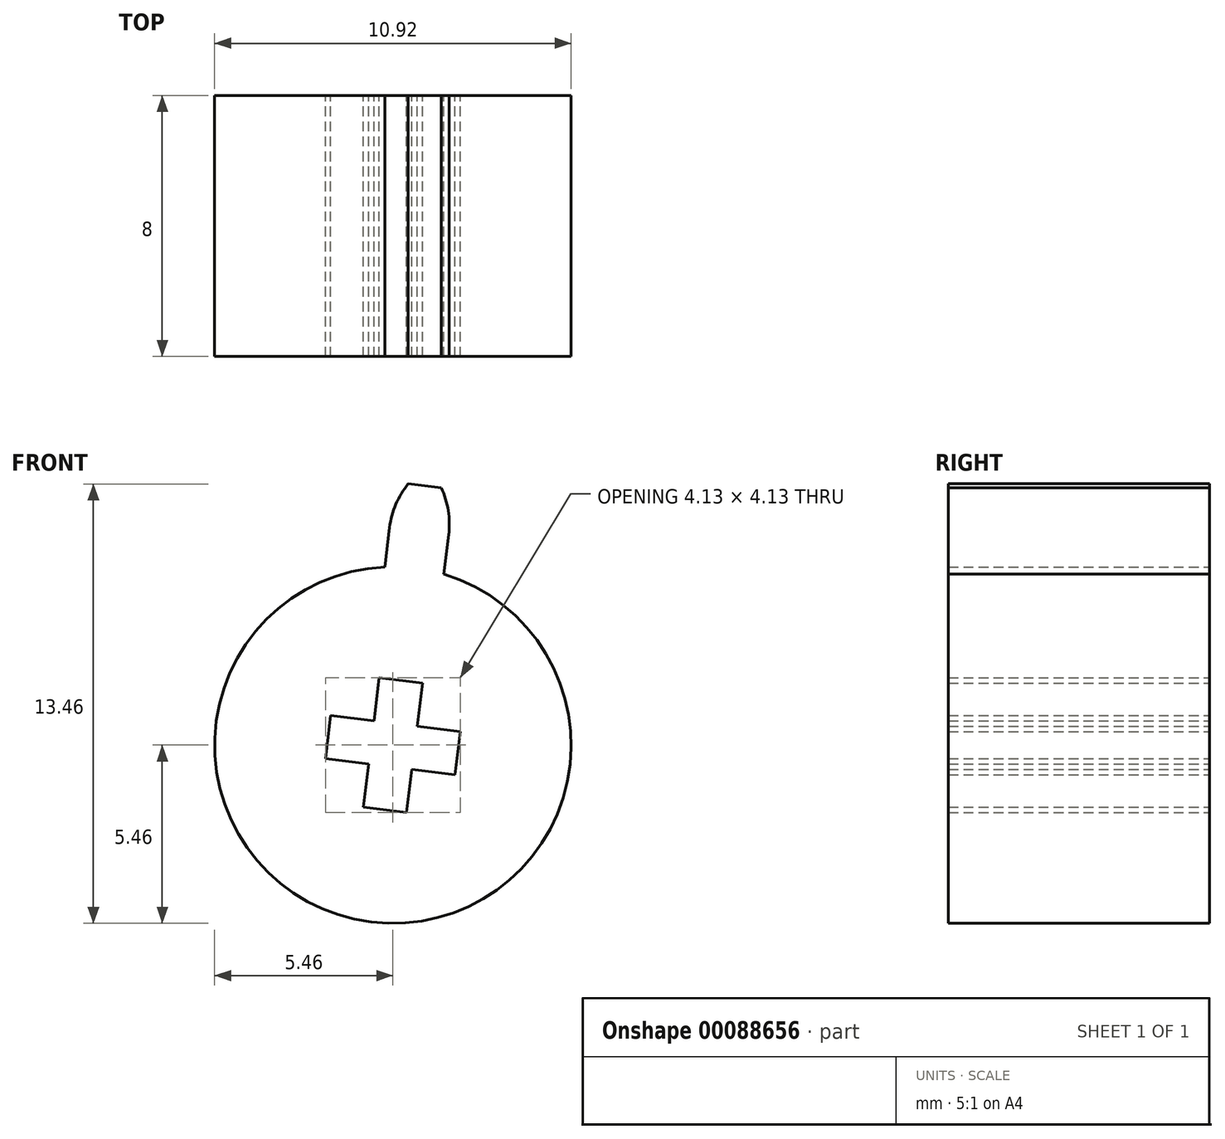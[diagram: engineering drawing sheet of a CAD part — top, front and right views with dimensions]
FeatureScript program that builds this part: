
annotation { "Feature Type Name" : "Feature", "Feature Type Description" : "" }
export const myFeature = defineFeature(function(context is Context, id is Id, definition is map)
    precondition{}
    {
        {
            var Q0;
            Q0=qCreatedBy(makeId("Front.planeOp"),FACE);
            var sketch = newSketch(context, id + "F0", { "sketchPlane" : qUnion([Q0])});
            skLineSegment(sketch, "E0", {"start": v(0.47, 8) * mm, "end": v(1.48, 7.88) * mm});
            skArc(sketch, "E1", {"start": v(-0.24, 5.45) * mm, "mid": v(0.67, 5.42) * mm, "end": v(1.56, 5.23) * mm});
            skLineSegment(sketch, "E2", {"start": v(-0.1, 6.67) * mm, "end": v(-0.24, 5.45) * mm});
            skLineSegment(sketch, "E3.MirrorCS", {"start": v(1.7, 6.44) * mm, "end": v(1.56, 5.23) * mm});
            skLineSegment(sketch, "E4", {"start": v(0.67, 5.42) * mm, "end": v(1.01, 8.23) * mm, "construction": true});
            skArc(sketch, "E5", {"start": v(0.47, 8) * mm, "mid": v(0.09, 7.37) * mm, "end": v(-0.1, 6.67) * mm});
            skArc(sketch, "E6", {"start": v(1.7, 6.44) * mm, "mid": v(1.7, 7.18) * mm, "end": v(1.48, 7.88) * mm});
            skSolve(sketch);
        }
        {
            var Q0;
            Q0=qCreatedBy(makeId("Top.planeOp"),FACE);
            var sketch = newSketch(context, id + "F1", { "sketchPlane" : qUnion([Q0])});
            skLineSegment(sketch, "E7", {"start": v(0, 0) * mm, "end": v(0, 30.53) * mm, "construction": true});
            skLineSegment(sketch, "E8", {"start": v(0, 0) * mm, "end": v(0, -25.91) * mm, "construction": true});
            skSolve(sketch);
        }
        {
            var Q0;
            Q0=qCreatedBy(makeId("Front.planeOp"),FACE);
            var sketch = newSketch(context, id + "F2", { "sketchPlane" : qUnion([Q0])});
            skCircle(sketch, "E9", {"center": v(0, 0) * mm, "radius": 5.46 * mm});
            skSolve(sketch);
        }
        {
            var Q0;
            Q0=makeQuery(id+"F2.imprint","IMPRINT",FACE,{"disambiguationData":[TD([[makeQuery(id+"F2.imprint","IMPRINT",EDGE,{"derivedFrom":sQuery(id+"F2.wireOp",EDGE,"E9")}),1.0]])]});
            extrude(context, id + "F3", {"entities" : qUnion([Q0]), "depth" : 8 * mm});
        }
        {
            var Q0;
            Q0=makeQuery(id+"F0.imprint","IMPRINT",FACE,{"disambiguationData":[TD([[makeQuery(id+"F0.imprint","IMPRINT",EDGE,{"derivedFrom":sQuery(id+"F0.wireOp",EDGE,"E0")}),-1.0]])]});
            var Q1;
            Q1=makeQuery(id+"F3.opExtrude","CAP_FACE",FACE,{"disambiguationData":[OSD([sQuery(id+"F2.wireOp",EDGE,"E9"),sQuery(id+"F2.wireOp",EDGE,"arTuxXPW-NgsZ-czPZ-2IIf-RW4LCaOOxTTB"),sQuery(id+"F2.wireOp",EDGE,"3ab69d48-fd6e-4c46-9385-d5405a46b24b.1.0.0"),sQuery(id+"F2.wireOp",EDGE,"6b936541-0af8-4921-b432-69622a55d935.0.1.0"),sQuery(id+"F2.wireOp",EDGE,"ef216592-30cf-427c-a956-27d8a622ba70.1.0.0")])],"isStart":false});
            extrude(context, id + "F4", {"entities" : qUnion([Q0]), "operationType" : NewBodyOperationType.ADD, "endBound" : BoundingType.UP_TO_SURFACE, "endBoundEntityFace" : qUnion([Q1]), "depth" : 25.4 * mm});
        }
        {
            var Q0;
            Q0=qCreatedBy(makeId("Front.planeOp"),FACE);
            var sketch = newSketch(context, id + "F5", { "sketchPlane" : qUnion([Q0])});
            skLineSegment(sketch, "E10", {"start": v(0.58, 4.76) * mm, "end": v(-0.4, -3.18) * mm, "construction": true});
            skLineSegment(sketch, "E11", {"start": v(0.9, 1.9) * mm, "end": v(0.74, 0.58) * mm});
            skLineSegment(sketch, "E12", {"start": v(0.74, 0.58) * mm, "end": v(2.07, 0.42) * mm});
            skLineSegment(sketch, "E13", {"start": v(2.07, 0.42) * mm, "end": v(1.99, -0.24) * mm});
            skLineSegment(sketch, "E14", {"start": v(0.9, 1.9) * mm, "end": v(0.24, 1.99) * mm});
            skPoint(sketch, "E15.0", {"position": v(-5.23, 1.56) * mm});
            skPoint(sketch, "E16.0", {"position": v(-5.45, -0.24) * mm});
            skLineSegment(sketch, "E17", {"start": v(-5.23, 1.56) * mm, "end": v(-5.45, -0.24) * mm, "construction": true});
            skPoint(sketch, "E18.0", {"position": v(-0.24, 5.45) * mm});
            skPoint(sketch, "E19.0", {"position": v(1.56, 5.23) * mm});
            skLineSegment(sketch, "E20", {"start": v(-0.24, 5.45) * mm, "end": v(1.56, 5.23) * mm, "construction": true});
            skLineSegment(sketch, "E21", {"start": v(0.66, 5.34) * mm, "end": v(0.58, 4.76) * mm, "construction": true});
            skLineSegment(sketch, "E22", {"start": v(-5.34, 0.66) * mm, "end": v(4.9, -0.6) * mm, "construction": true});
            skLineSegment(sketch, "E23.MirrorCS", {"start": v(1.9, -0.9) * mm, "end": v(1.99, -0.24) * mm});
            skLineSegment(sketch, "E24.MirrorCS", {"start": v(0.58, -0.74) * mm, "end": v(1.9, -0.9) * mm});
            skLineSegment(sketch, "E25.MirrorCS", {"start": v(0.42, -2.07) * mm, "end": v(0.58, -0.74) * mm});
            skLineSegment(sketch, "E26.MirrorCS", {"start": v(0.42, -2.07) * mm, "end": v(-0.24, -1.99) * mm});
            skLineSegment(sketch, "E27.MirrorCS", {"start": v(-0.9, -1.9) * mm, "end": v(-0.24, -1.99) * mm});
            skLineSegment(sketch, "E28.MirrorCS", {"start": v(-0.9, -1.9) * mm, "end": v(-0.74, -0.58) * mm});
            skLineSegment(sketch, "E29.MirrorCS", {"start": v(-0.74, -0.58) * mm, "end": v(-2.07, -0.42) * mm});
            skLineSegment(sketch, "E30.MirrorCS", {"start": v(-2.07, -0.42) * mm, "end": v(-1.99, 0.24) * mm});
            skLineSegment(sketch, "E31.MirrorCS", {"start": v(-1.9, 0.9) * mm, "end": v(-1.99, 0.24) * mm});
            skLineSegment(sketch, "E32.MirrorCS", {"start": v(-0.58, 0.74) * mm, "end": v(-1.9, 0.9) * mm});
            skLineSegment(sketch, "E33.MirrorCS", {"start": v(-0.42, 2.07) * mm, "end": v(-0.58, 0.74) * mm});
            skLineSegment(sketch, "E34.MirrorCS", {"start": v(-0.42, 2.07) * mm, "end": v(0.24, 1.99) * mm});
            skSolve(sketch);
        }
        {
            var Q0;
            Q0 = qSketchRegion(id + "F5", true);
            extrude(context, id + "F6", {"entities" : qUnion([Q0]), "operationType" : NewBodyOperationType.REMOVE, "depth" : 25.4 * mm});
        }
    });
